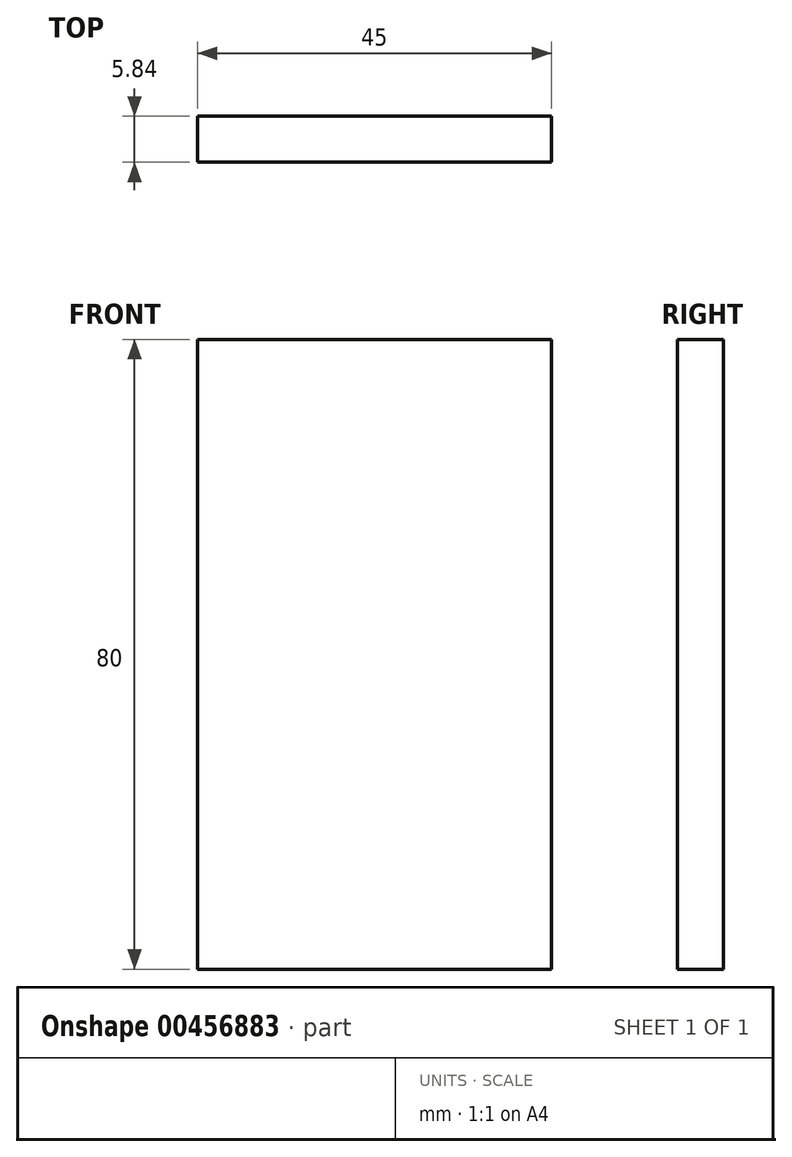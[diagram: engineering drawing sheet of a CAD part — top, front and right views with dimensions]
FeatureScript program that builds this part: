
annotation { "Feature Type Name" : "Feature", "Feature Type Description" : "" }
export const myFeature = defineFeature(function(context is Context, id is Id, definition is map)
    precondition{}
    {
        {
            var Q0;
            Q0=qCreatedBy(makeId("Front.planeOp"),FACE);
            var sketch = newSketch(context, id + "F0", { "sketchPlane" : qUnion([Q0])});
            skLineSegment(sketch, "E0.bottom", {"start": v(-22.7, 80) * mm, "end": v(22.3, 80) * mm});
            skLineSegment(sketch, "E0.top", {"start": v(-22.7, 0) * mm, "end": v(22.3, 0) * mm});
            skLineSegment(sketch, "E0.left", {"start": v(-22.7, 80) * mm, "end": v(-22.7, 0) * mm});
            skLineSegment(sketch, "E0.right", {"start": v(22.3, 80) * mm, "end": v(22.3, 0) * mm});
            skSolve(sketch);
        }
        {
            var Q0;
            Q0 = qSketchRegion(id + "F0", true);
            extrude(context, id + "F1", {"entities" : qUnion([Q0]), "depth" : 5.84 * mm});
        }
    });
